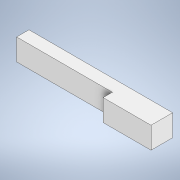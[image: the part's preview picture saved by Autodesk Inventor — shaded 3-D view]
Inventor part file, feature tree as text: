
AUTODESK INVENTOR PART (.ipt)
format: ipt  version: 2021 (Build 250183000, 183)  size: 100,352 bytes
history: native  units: in
note: dims shown in document units (in); Inventor stores cm internally (conversion verified against a paired STEP export)
features: extrude x1, sketch x1
ambient origin geometry x8: Origin, YZ Plane, XZ Plane, XY Plane, X Axis, Y Axis, Z Axis, Center Point
bodies: Solid1 (feature_tree)
feature tree (2):
  extrude  "Extrusion1"  Depth=3.875in
  sketch  "Sketch1"  dims[d0=5.8125in d1=3.875in d2=0.875in d3=0.5in d4=0.875in d5=0.0in]
